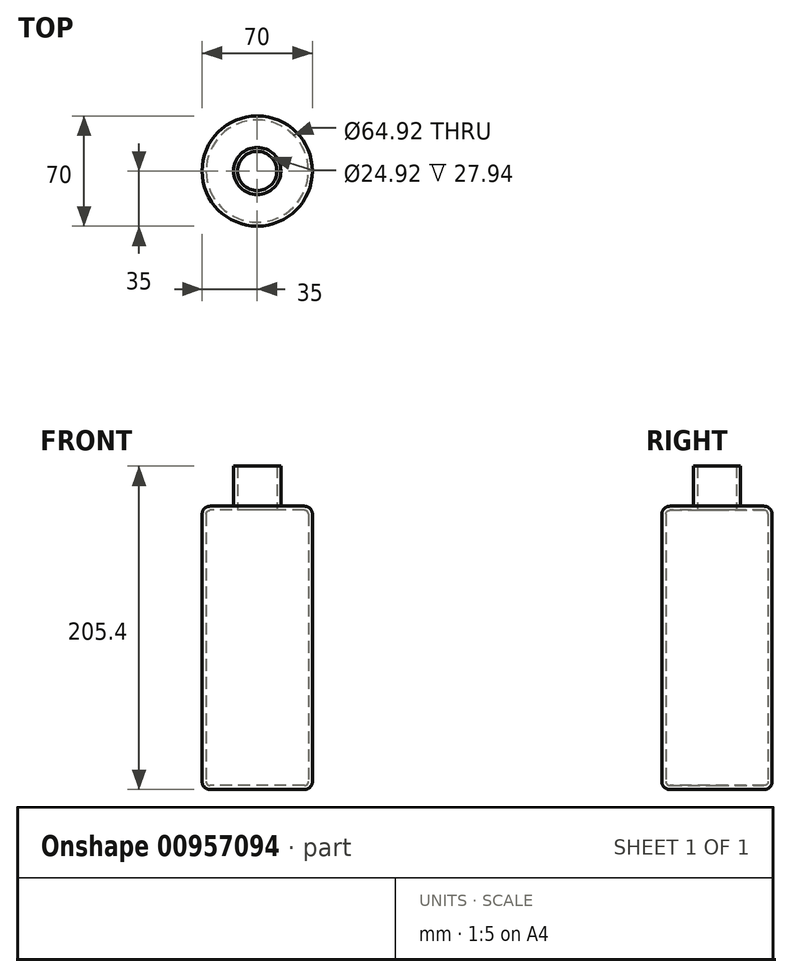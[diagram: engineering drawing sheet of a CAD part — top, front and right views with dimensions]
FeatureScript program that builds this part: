
annotation { "Feature Type Name" : "Feature", "Feature Type Description" : "" }
export const myFeature = defineFeature(function(context is Context, id is Id, definition is map)
    precondition{}
    {
        {
            var Q0;
            Q0=qCreatedBy(makeId("Top.planeOp"),FACE);
            var sketch = newSketch(context, id + "F0", { "sketchPlane" : qUnion([Q0])});
            skCircle(sketch, "E0", {"center": v(0, 0) * mm, "radius": 35 * mm});
            skSolve(sketch);
        }
        {
            var Q0;
            Q0 = qSketchRegion(id + "F0", true);
            extrude(context, id + "F1", {"entities" : qUnion([Q0]), "depth" : 180 * mm, "offsetDistance" : 25.4 * mm});
        }
        {
            var Q0;
            Q0=makeQuery(id+"F1.opExtrude","CAP_FACE",FACE,{"disambiguationData":[OSD([sQuery(id+"F0.wireOp",EDGE,"E0")])],"isStart":false});
            var sketch = newSketch(context, id + "F2", { "sketchPlane" : qUnion([Q0])});
            skCircle(sketch, "E1", {"center": v(0, 0) * mm, "radius": 15 * mm});
            skSolve(sketch);
        }
        {
            var Q0;
            Q0=makeQuery(id+"F2.imprint","IMPRINT",FACE,{"disambiguationData":[TD([[makeQuery(id+"F2.imprint","IMPRINT",EDGE,{"derivedFrom":sQuery(id+"F2.wireOp",EDGE,"E1")}),1.0]])]});
            extrude(context, id + "F3", {"entities" : qUnion([Q0]), "operationType" : NewBodyOperationType.ADD, "depth" : 25.4 * mm, "offsetDistance" : 25.4 * mm});
        }
        {
            var Q0;
            Q0=makeQuery(id+"F1.opExtrude","CAP_EDGE",EDGE,{"disambiguationData":[OSD([sQuery(id+"F0.wireOp",EDGE,"E0")])],"isStart":false});
            fillet(context, id + "F4", {"entities" : qUnion([Q0]), "radius" : 5.08 * mm, "tangentPropagation" : true, "allowEdgeOverflow" : false});
        }
        {
            var Q0;
            Q0=makeQuery(id+"F1.opExtrude","CAP_EDGE",EDGE,{"disambiguationData":[OSD([sQuery(id+"F0.wireOp",EDGE,"E0")])],"isStart":true});
            var Q1;
            Q1=makeQuery(id+"F3.opExtrude","CAP_EDGE",EDGE,{"disambiguationData":[OSD([sQuery(id+"F2.wireOp",EDGE,"E1")])],"isStart":true});
            fillet(context, id + "F5", {"entities" : qUnion([Q0, Q1]), "radius" : 5.08 * mm, "tangentPropagation" : true, "allowEdgeOverflow" : false});
        }
        {
            var Q0;
            Q0=makeQuery(id+"F1.opExtrude","CAP_FACE",FACE,{"disambiguationData":[OSD([sQuery(id+"F0.wireOp",EDGE,"E0")])],"isStart":true});
            var sketch = newSketch(context, id + "F6", { "sketchPlane" : qUnion([Q0])});
            skCircle(sketch, "E2", {"center": v(0, 0) * mm, "radius": 14.57 * mm});
            skSolve(sketch);
        }
        {
            var Q0;
            Q0=makeQuery(id+"F6.imprint","IMPRINT",FACE,{"disambiguationData":[TD([[makeQuery(id+"F6.imprint","IMPRINT",EDGE,{"derivedFrom":sQuery(id+"F6.wireOp",EDGE,"E2")}),1.0]])]});
            var Q1;
            Q1=makeQuery(id+"F6.imprint","IMPRINT",FACE,{"disambiguationData":[TD([[makeQuery(id+"F6.imprint","IMPRINT",EDGE,{"derivedFrom":sQuery(id+"F6.wireOp",EDGE,"E2")}),-1.0]])]});
            extrude(context, id + "F7", {"entities" : qUnion([Q0, Q1]), "operationType" : NewBodyOperationType.ADD, "oppositeDirection" : true, "depth" : 6.86 * mm, "offsetDistance" : 25.4 * mm});
        }
        {
            var Q0;
            Q0=makeQuery(id+"F3.opExtrude","CAP_FACE",FACE,{"disambiguationData":[OSD([sQuery(id+"F2.wireOp",EDGE,"E1")])],"isStart":false});
            shell(context, id + "F8", {"entities" : qUnion([Q0]), "thickness" : 2.54 * mm});
        }
    });
